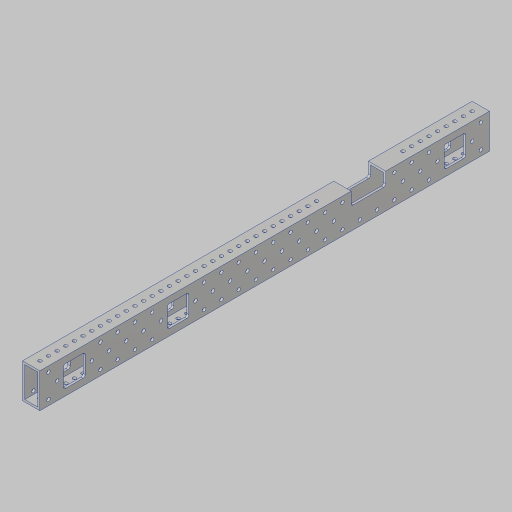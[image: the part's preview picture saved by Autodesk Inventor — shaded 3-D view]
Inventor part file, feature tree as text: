
AUTODESK INVENTOR PART (.ipt)
format: ipt  version: 2023.5 (Build 275446000, 446)  size: 452,096 bytes
history: native  units: in
note: dims shown in document units (in); Inventor stores cm internally (conversion verified against a paired STEP export)
features: sketch x4, extrude x3, hole x2, fillet x2, projected_geometry x1
ambient origin geometry x8: Origin, YZ Plane, XZ Plane, XY Plane, X Axis, Y Axis, Z Axis, Center Point
bodies: Solid1 (feature_tree)
feature tree (12):
  extrude  "Extrusion1"  Depth=1.0in
  hole  "Hole1"  [1 undecoded]
  hole  "Hole2"  [1 undecoded]
  extrude  "Extrusion3"  Depth=0.375in
  fillet  "Fillet1"  Radius=1.0in
  extrude  "Extrusion4"  Depth=1.0in
  fillet  "Fillet2"  Radius=1.0in
  sketch  "Sketch2"  dims[d4=0.0in d6=1.0in]
  sketch  "Sketch3"  dims[d7=9.8425in d9=0.5in d10=0.3937in d12=1.0in d14=9.8425in d16=0.5in d17=0.3937in d19=1.0in]
  sketch  "Sketch5"  dims[d21=0.201in d22=0.75in d23=0.385in d24=0.25in d25=0.5635in d26=1.0in d27=0.8108in d28=0.5in]
  sketch  "Sketch6"  dims[d29=0.375in d30=0.375in d31=1.0in d32=5.1181in d34=1.0in d35=0.3937in d37=1.0in d39=5.1181in d41=1.0in d42=0.3937in d44=1.0in d46=0.201in d47=0.75in d48=0.375in d49=0.25in d50=0.5635in d51=1.0in d52=0.8108in d59=1.25in d60=1.25in d61=1.0in d62=0.0in d63=0.125in d64=6.0in d66=0.75in d67=2.0in d69=1.0in d70=0.0in d71=0.125in d72=0.0in d73=0.0in d74=0.0in d75=0.0in]
  projected_geometry  "Project Cut Edges1"
note: 2 required parameter values undecoded (feature->parameter linkage not recoverable at this tier; creation-order binding heuristic only, values carry confidence <= 0.55)
